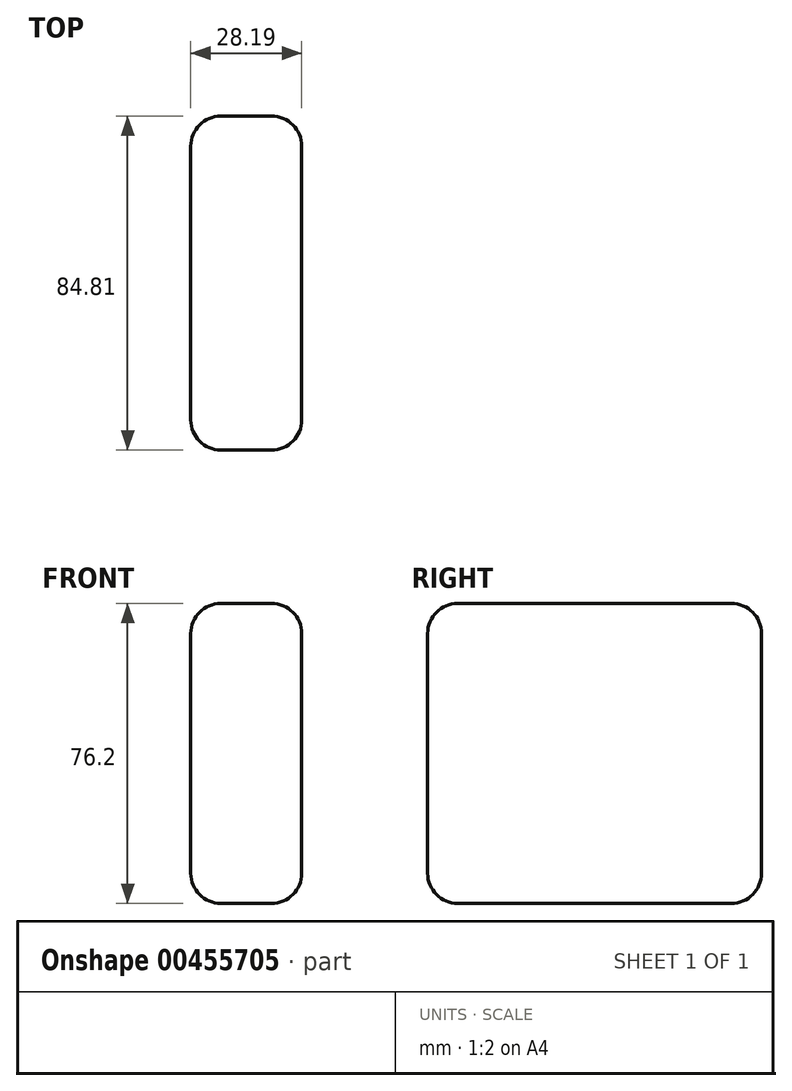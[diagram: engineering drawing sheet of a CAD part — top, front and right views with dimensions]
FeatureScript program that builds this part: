
annotation { "Feature Type Name" : "Feature", "Feature Type Description" : "" }
export const myFeature = defineFeature(function(context is Context, id is Id, definition is map)
    precondition{}
    {
        {
            var Q0;
            Q0=qCreatedBy(makeId("Top.planeOp"),FACE);
            var sketch = newSketch(context, id + "F0", { "sketchPlane" : qUnion([Q0])});
            skLineSegment(sketch, "E0.bottom", {"start": v(-38.05, 41.06) * mm, "end": v(-66.24, 41.06) * mm});
            skLineSegment(sketch, "E0.top", {"start": v(-38.05, -43.75) * mm, "end": v(-66.24, -43.75) * mm});
            skLineSegment(sketch, "E0.left", {"start": v(-38.05, 41.06) * mm, "end": v(-38.05, -43.75) * mm});
            skLineSegment(sketch, "E0.right", {"start": v(-66.24, 41.06) * mm, "end": v(-66.24, -43.75) * mm});
            skSolve(sketch);
        }
        {
            var Q0;
            Q0=makeQuery(id+"F0.imprint","IMPRINT",FACE,{"disambiguationData":[TD([[makeQuery(id+"F0.imprint","IMPRINT",EDGE,{"derivedFrom":sQuery(id+"F0.wireOp",EDGE,"E0.bottom")}),1.0]])]});
            extrude(context, id + "F1", {"entities" : qUnion([Q0]), "depth" : 76.2 * mm});
        }
        {
            var Q0;
            Q0=makeQuery(id+"F1.opExtrude","SWEPT_EDGE",EDGE,{"disambiguationData":[OSD([sQuery(id+"F0.wireOp",EDGE,"E0.bottom"),sQuery(id+"F0.wireOp",EDGE,"E0.right")])]});
            var Q1;
            Q1=makeQuery(id+"F1.opExtrude","SWEPT_EDGE",EDGE,{"disambiguationData":[OSD([sQuery(id+"F0.wireOp",EDGE,"E0.top"),sQuery(id+"F0.wireOp",EDGE,"E0.right")])]});
            var Q2;
            Q2=makeQuery(id+"F1.opExtrude","SWEPT_EDGE",EDGE,{"disambiguationData":[OSD([sQuery(id+"F0.wireOp",EDGE,"E0.top"),sQuery(id+"F0.wireOp",EDGE,"E0.left")])]});
            var Q3;
            Q3=makeQuery(id+"F1.opExtrude","SWEPT_EDGE",EDGE,{"disambiguationData":[OSD([sQuery(id+"F0.wireOp",EDGE,"E0.bottom"),sQuery(id+"F0.wireOp",EDGE,"E0.left")])]});
            fillet(context, id + "F2", {"entities" : qUnion([Q0, Q1, Q2, Q3]), "radius" : 7.62 * mm, "tangentPropagation" : true, "allowEdgeOverflow" : false});
        }
        {
            var Q0;
            Q0=makeQuery(id+"F1.opExtrude","CAP_EDGE",EDGE,{"disambiguationData":[OSD([sQuery(id+"F0.wireOp",EDGE,"E0.left")])],"isStart":false});
            var Q1;
            Q1=makeQuery(id+"F1.opExtrude","CAP_EDGE",EDGE,{"disambiguationData":[OSD([sQuery(id+"F0.wireOp",EDGE,"E0.right")])],"isStart":false});
            var Q2;
            Q2=makeQuery(id+"F1.opExtrude","CAP_EDGE",EDGE,{"disambiguationData":[OSD([sQuery(id+"F0.wireOp",EDGE,"E0.right")])],"isStart":true});
            var Q3;
            Q3=makeQuery(id+"F1.opExtrude","CAP_EDGE",EDGE,{"disambiguationData":[OSD([sQuery(id+"F0.wireOp",EDGE,"E0.left")])],"isStart":true});
            fillet(context, id + "F3", {"entities" : qUnion([Q0, Q1, Q2, Q3]), "radius" : 7.62 * mm, "tangentPropagation" : true, "allowEdgeOverflow" : false});
        }
    });
